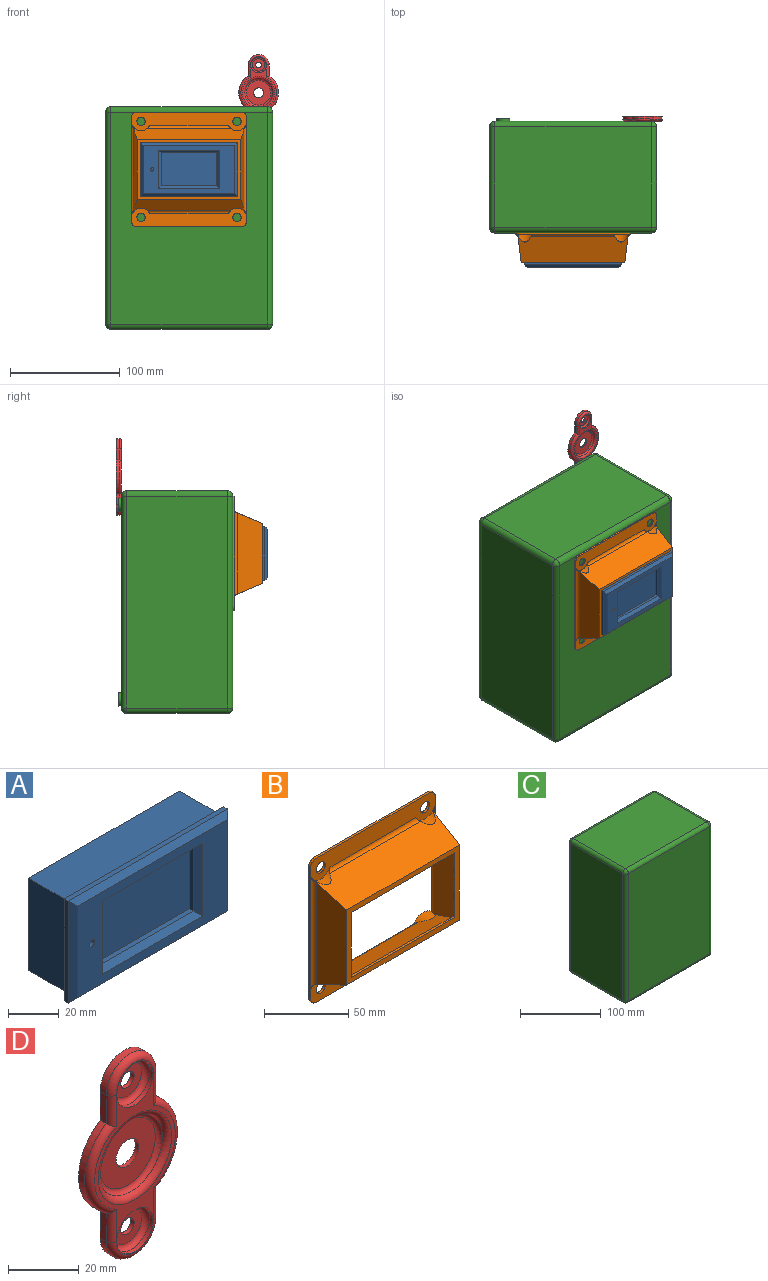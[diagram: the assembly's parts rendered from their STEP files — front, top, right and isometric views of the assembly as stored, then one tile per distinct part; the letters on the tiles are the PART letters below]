
ASSEMBLY  parts=4 mates=3
PART A: 26 faces, bbox 88.9x27x49.2 mm
  f0: plane 88.9x49.21mm, normal (0,1,0), area 635.1mm2, adj f2,f3,f4,f5,f12,f13,f14,f15
  f1: plane 83.82x44.13mm, normal (0,-1,0), area 1721.9mm2, adj f6,f18,f19,f20,f21,f22,f23,f24
  f2: plane 88.9x2.22mm, normal (0,0,1), area 197.6mm2, adj f0,f3,f5,f18
  f3: plane 49.21x2.22mm, normal (-1,0,0), area 109.4mm2, adj f0,f2,f4,f19
  f4: plane 88.9x2.22mm, normal (0,0,-1), area 197.6mm2, adj f0,f3,f5,f21
  f5: plane 49.21x2.22mm, normal (1,0,0), area 109.4mm2, adj f0,f2,f4,f20
  f6: cylinder r=1.59mm len=4.76mm, axis (0,-1,0), area 47.5mm2, adj f1,f17
  f7: plane 50.8x2.22mm, normal (0,0,-1), area 112.9mm2, adj f8,f10,f16,f22
  f8: plane 30.16x2.22mm, normal (1,0,0), area 67mm2, adj f7,f9,f16,f23
  f9: plane 50.8x2.22mm, normal (0,0,1), area 112.9mm2, adj f8,f10,f16,f25
  f10: plane 30.16x2.22mm, normal (-1,0,0), area 67mm2, adj f7,f9,f16,f24
  f11: plane 84.14x44.45mm, normal (0,1,0), area 3739.9mm2, adj f12,f13,f14,f15
  f12: plane 44.45x22.23mm, normal (-1,0,0), area 987.9mm2, adj f0,f11,f13,f15
  f13: plane 84.14x22.23mm, normal (0,0,-1), area 1870mm2, adj f0,f11,f12,f14
  f14: plane 44.45x22.23mm, normal (1,0,0), area 987.9mm2, adj f0,f11,f13,f15
  f15: plane 84.14x22.23mm, normal (0,0,1), area 1870mm2, adj f0,f11,f12,f14
  f16: plane 50.8x30.16mm, normal (0,-1,0), area 1532.3mm2, adj f7,f8,f9,f10
  f17: plane 3.18x3.18mm, normal (0,-1,0), area 7.9mm2, adj f6
  f18: plane 88.9x2.54mm, normal (0,-0.71,0.71), area 310.2mm2, adj f1,f2,f19,f20
  f19: plane 49.21x2.54mm, normal (-0.71,-0.71,0), area 167.7mm2, adj f1,f3,f18,f21
  f20: plane 49.21x2.54mm, normal (0.71,-0.71,0), area 167.7mm2, adj f1,f5,f18,f21
  f21: plane 88.9x2.54mm, normal (0,-0.71,-0.71), area 310.2mm2, adj f1,f4,f19,f20
  f22: plane 55.88x2.54mm, normal (0,-0.71,-0.71), area 191.6mm2, adj f1,f7,f23,f24
  f23: plane 35.24x2.54mm, normal (0.71,-0.71,0), area 117.5mm2, adj f1,f8,f22,f25
  f24: plane 35.24x2.54mm, normal (-0.71,-0.71,0), area 117.5mm2, adj f1,f10,f22,f25
  f25: plane 55.88x2.54mm, normal (0,-0.71,0.71), area 191.6mm2, adj f1,f9,f23,f24
PART B: 80 faces, bbox 104.8x27x104.8 mm
  f0: plane 87.76x19.75mm, normal (0,1,0), area 117.5mm2, adj f1,f62,f63,f64,f65,f67,f68,f73
  f1: plane 47.1x1.6mm, normal (1,0,0), area 70.4mm2, adj f0,f2,f3,f61,f63,f68,f69,f71
  f2: plane 94.6x54.6mm, normal (0,-1,0), area 1062.7mm2, adj f1,f9,f10,f21,f22,f61,f62,f63
  f3: plane 87.76x19.75mm, normal (0,1,0), area 117.5mm2, adj f1,f61,f62,f64,f66,f67,f69,f72
  f4: plane 8.2x8.2mm, normal (0,1,0), area 8.6mm2, adj f49,f77
  f5: plane 104.78x104.78mm, normal (0,1,0), area 648.7mm2, adj f13,f14,f15,f16,f17,f18,f19,f20
  f6: plane 8.2x8.2mm, normal (0,1,0), area 8.6mm2, adj f50,f79
  f7: plane 8.2x8.2mm, normal (0,1,0), area 8.6mm2, adj f51,f78
  f8: plane 104.78x17.23mm, normal (0,-1,0), area 1299.9mm2, adj f13,f14,f15,f17,f18,f25,f26,f29
  f9: plane 100.53x23.58mm, normal (0,-0.39,-0.92), area 2410.4mm2, adj f2,f21,f22,f25,f26,f28,f29,f30
  f10: plane 100.53x23.58mm, normal (0,-0.39,0.92), area 2410.4mm2, adj f2,f21,f22,f23,f24,f27,f28,f31
  f11: plane 104.78x17.23mm, normal (0,-1,0), area 1299.9mm2, adj f13,f15,f16,f19,f20,f23,f24,f27
  f12: plane 8.2x8.2mm, normal (0,1,0), area 8.6mm2, adj f48,f76
  f13: plane 94.78x1.6mm, normal (-1,0,0), area 151.6mm2, adj f5,f8,f11,f17,f20,f34
  f14: plane 94.78x1.6mm, normal (0,0,-1), area 151.6mm2, adj f5,f8,f17,f18
  f15: plane 94.78x1.6mm, normal (1,0,0), area 151.6mm2, adj f5,f8,f11,f18,f19,f28
  f16: plane 94.78x1.6mm, normal (0,0,1), area 151.6mm2, adj f5,f11,f19,f20
  f17: cylinder r=5mm len=5mm, axis (0,-1,0), area 12.6mm2, adj f5,f8,f13,f14
  f18: cylinder r=5mm len=5mm, axis (0,1,0), area 12.6mm2, adj f5,f8,f14,f15
  f19: cylinder r=5mm len=5mm, axis (0,-1,0), area 12.6mm2, adj f5,f11,f15,f16
  f20: cylinder r=5mm len=5mm, axis (0,1,0), area 12.6mm2, adj f5,f11,f13,f16
  f21: plane 74.02x22.84mm, normal (0.99,-0.12,0), area 1479.5mm2, adj f2,f9,f10,f28
  f22: plane 74.02x22.84mm, normal (-0.99,-0.12,0), area 1479.5mm2, adj f2,f9,f10,f34
  f23: cylinder r=8.61mm len=15.56mm, axis (0,1,0), area 68.5mm2, adj f10,f11,f27,f31
  f24: cylinder r=8.61mm len=15.56mm, axis (0,1,0), area 68.5mm2, adj f10,f11,f31,f32
  f25: cylinder r=8.61mm len=15.56mm, axis (0,1,0), area 68.5mm2, adj f8,f9,f30,f33
  f26: cylinder r=8.61mm len=15.56mm, axis (0,1,0), area 68.5mm2, adj f8,f9,f29,f30
  f27: cylinder r=3mm len=2.91mm, axis (-1,0,0), area 2.8mm2, adj f10,f11,f23,f28
  f28: cylinder r=3mm len=80.17mm, axis (0,0,-1), area 280.1mm2, adj f9,f10,f15,f21,f27,f29
  f29: cylinder r=3mm len=2.91mm, axis (1,0,0), area 2.8mm2, adj f8,f9,f26,f28
  f30: cylinder r=3mm len=76.14mm, axis (1,0,0), area 259.7mm2, adj f8,f9,f25,f26
  f31: cylinder r=3mm len=76.14mm, axis (-1,0,0), area 259.7mm2, adj f10,f11,f23,f24
  f32: cylinder r=3mm len=2.91mm, axis (-1,0,0), area 2.8mm2, adj f10,f11,f24,f34
  f33: cylinder r=3mm len=2.91mm, axis (1,0,0), area 2.8mm2, adj f8,f9,f25,f34
  f34: cylinder r=3mm len=80.17mm, axis (0,0,-1), area 280.1mm2, adj f9,f10,f13,f22,f32,f33
  f35: plane 101.58x17.23mm, normal (0,1,0), area 1146mm2, adj f36,f37,f43,f46,f47,f49,f51,f54
  f36: plane 94.78x0.52mm, normal (1,0,0), area 38mm2, adj f5,f35,f39,f44,f47,f55,f56,f60
  f37: plane 94.78x0.52mm, normal (-1,0,0), area 38mm2, adj f5,f35,f38,f39,f45,f46,f54,f57
  f38: cylinder r=4.6mm len=72.7mm, axis (0,0,-1), area 303.3mm2, adj f37,f52,f54,f57
  f39: plane 101.58x17.23mm, normal (0,1,0), area 1146mm2, adj f36,f37,f42,f44,f45,f48,f50,f56
  f40: plane 96.55x21.23mm, normal (0,0.39,0.92), area 2085.9mm2, adj f52,f53,f56,f57,f58,f64,f66,f67
  f41: plane 96.55x21.23mm, normal (0,0.39,-0.92), area 2085.9mm2, adj f52,f53,f54,f55,f59,f64,f65,f67
  f42: plane 94.78x0mm, normal (0,0,1), area 0mm2, adj f5,f39,f44,f45
  f43: plane 94.78x0mm, normal (0,0,-1), area 0mm2, adj f5,f35,f46,f47
  f44: cylinder r=3.4mm len=3.4mm, axis (0,-1,0), area 0mm2, adj f5,f36,f39,f42
  f45: cylinder r=3.4mm len=3.4mm, axis (0,1,0), area 0mm2, adj f5,f37,f39,f42
  f46: cylinder r=3.4mm len=3.4mm, axis (0,-1,0), area 0mm2, adj f5,f35,f37,f43
  f47: cylinder r=3.4mm len=3.4mm, axis (0,1,0), area 0mm2, adj f5,f35,f36,f43
  f48: cylinder r=4.1mm len=8.2mm, axis (0,-1,0), area 0mm2, adj f12,f39
  f49: cylinder r=4.1mm len=8.2mm, axis (0,-1,0), area 0mm2, adj f4,f35
  f50: cylinder r=4.1mm len=8.2mm, axis (0,-1,0), area 0mm2, adj f6,f39
  f51: cylinder r=4.1mm len=8.2mm, axis (0,-1,0), area 0mm2, adj f7,f35
  f52: plane 69.44x19.45mm, normal (-0.99,0.12,0), area 1221.9mm2, adj f38,f40,f41,f54,f57,f64
  f53: plane 69.44x19.45mm, normal (0.99,0.12,0), area 1221.9mm2, adj f40,f41,f55,f56,f60,f67
  f54: cylinder r=10.21mm len=16.53mm, axis (0,1,0), area 88.9mm2, adj f35,f37,f38,f41,f52,f59
  f55: cylinder r=10.21mm len=16.53mm, axis (0,1,0), area 88.9mm2, adj f35,f36,f41,f53,f59,f60
  f56: cylinder r=10.21mm len=16.53mm, axis (0,1,0), area 88.9mm2, adj f36,f39,f40,f53,f58,f60
  f57: cylinder r=10.21mm len=16.53mm, axis (0,1,0), area 88.9mm2, adj f37,f38,f39,f40,f52,f58
  f58: cylinder r=4.6mm len=74.67mm, axis (1,0,0), area 384.1mm2, adj f39,f40,f56,f57
  f59: cylinder r=4.6mm len=74.67mm, axis (-1,0,0), area 384.1mm2, adj f35,f41,f54,f55
  f60: cylinder r=4.6mm len=72.7mm, axis (0,0,-1), area 303.3mm2, adj f36,f53,f55,f56
  f61: plane 87.1x1.6mm, normal (0,0,1), area 139.4mm2, adj f1,f2,f3,f62
  f62: plane 47.1x1.6mm, normal (-1,0,0), area 70.4mm2, adj f0,f2,f3,f61,f63,f72,f73,f75
  f63: plane 87.1x1.6mm, normal (0,0,-1), area 139.4mm2, adj f0,f1,f2,f62
  f64: plane 54.17x2.24mm, normal (-0.66,0.75,0), area 134.3mm2, adj f0,f3,f40,f41,f52,f65,f66,f72
  f65: plane 90.87x2.08mm, normal (0,0.83,-0.55), area 222.5mm2, adj f0,f41,f64,f67
  f66: plane 90.87x2.08mm, normal (0,0.83,0.55), area 222.5mm2, adj f3,f40,f64,f67
  f67: plane 54.17x2.24mm, normal (0.66,0.75,0), area 134.3mm2, adj f0,f3,f40,f41,f53,f65,f66,f68
  f68: plane 2x1.98mm, normal (0,0,-1), area 2.2mm2, adj f0,f1,f67,f70,f71
  f69: plane 2x1.98mm, normal (0,0,1), area 2.2mm2, adj f1,f3,f67,f70,f71
  f70: plane 10x1.98mm, normal (1,0,0), area 19.8mm2, adj f67,f68,f69,f71
  f71: plane 10x2mm, normal (0,1,0), area 20mm2, adj f1,f68,f69,f70
  f72: plane 2x1.98mm, normal (0,0,1), area 2.2mm2, adj f3,f62,f64,f74,f75
  f73: plane 2x1.98mm, normal (0,0,-1), area 2.2mm2, adj f0,f62,f64,f74,f75
  f74: plane 10x1.98mm, normal (-1,0,0), area 19.8mm2, adj f64,f72,f73,f75
  f75: plane 10x2mm, normal (0,1,0), area 20mm2, adj f62,f72,f73,f74
  f76: cylinder r=3.75mm len=7.5mm, axis (0,-1,0), area 37.7mm2, adj f8,f12
  f77: cylinder r=3.75mm len=7.5mm, axis (0,-1,0), area 37.7mm2, adj f4,f11
  f78: cylinder r=3.75mm len=7.5mm, axis (0,-1,0), area 37.7mm2, adj f7,f11
  f79: cylinder r=3.75mm len=7.5mm, axis (0,-1,0), area 37.7mm2, adj f6,f8
PART C: 42 faces, bbox 152.4x104.6x203.2 mm
  f0: plane 193.2x91.6mm, normal (-1,0,0), area 17697.1mm2, adj f30,f35,f38,f41
  f1: plane 142.4x91.6mm, normal (0,0,-1), area 13043.8mm2, adj f27,f36,f37,f41
  f2: plane 193.2x91.6mm, normal (1,0,0), area 17697.1mm2, adj f22,f26,f27,f28
  f3: plane 142.4x91.6mm, normal (0,0,1), area 13043.8mm2, adj f22,f25,f29,f30
  f4: plane 193.2x142.4mm, normal (0,-1,0), area 27511.7mm2, adj f25,f26,f35,f36
  f5: plane 193.2x142.4mm, normal (0,1,0), area 27059.3mm2, adj f7,f10,f14,f19,f28,f29,f37,f38
  f6: cylinder r=1.59mm len=3.18mm, axis (0,-1,0), area 29.9mm2, adj f8,f9
  f7: cylinder r=6mm len=12mm, axis (0,-1,0), area 113.1mm2, adj f5,f8
  f8: plane 12x12mm, normal (0,1,0), area 105.2mm2, adj f6,f7
  f9: plane 3.18x3.18mm, normal (0,1,0), area 7.9mm2, adj f6
  f10: cylinder r=6mm len=12mm, axis (0,-1,0), area 113.1mm2, adj f5,f12
  f11: cylinder r=1.59mm len=3.18mm, axis (0,-1,0), area 29.9mm2, adj f12,f13
  f12: plane 12x12mm, normal (0,1,0), area 105.2mm2, adj f10,f11
  f13: plane 3.18x3.18mm, normal (0,1,0), area 7.9mm2, adj f11
  f14: cylinder r=6mm len=12mm, axis (0,-1,0), area 113.1mm2, adj f5,f16
  f15: cylinder r=1.59mm len=3.18mm, axis (0,-1,0), area 29.9mm2, adj f16,f17
  f16: plane 12x12mm, normal (0,1,0), area 105.2mm2, adj f14,f15
  f17: plane 3.18x3.18mm, normal (0,1,0), area 7.9mm2, adj f15
  f18: cylinder r=1.59mm len=3.18mm, axis (0,-1,0), area 29.9mm2, adj f20,f21
  f19: cylinder r=6mm len=12mm, axis (0,-1,0), area 113.1mm2, adj f5,f20
  f20: plane 12x12mm, normal (0,1,0), area 105.2mm2, adj f18,f19
  f21: plane 3.18x3.18mm, normal (0,1,0), area 7.9mm2, adj f18
  f22: cylinder r=5mm len=91.6mm, axis (0,-1,0), area 719.4mm2, adj f2,f3,f23,f24
  f23: sphere r=5mm, area 39.3mm2, adj f22,f25,f26
  f24: sphere r=5mm, area 39.3mm2, adj f22,f28,f29
  f25: cylinder r=5mm len=142.4mm, axis (1,0,0), area 1118.4mm2, adj f3,f4,f23,f31
  f26: cylinder r=5mm len=193.2mm, axis (0,0,-1), area 1517.4mm2, adj f2,f4,f23,f32
  f27: cylinder r=5mm len=91.6mm, axis (0,1,0), area 719.4mm2, adj f1,f2,f32,f33
  f28: cylinder r=5mm len=193.2mm, axis (0,0,1), area 1517.4mm2, adj f2,f5,f24,f33
  f29: cylinder r=5mm len=142.4mm, axis (-1,0,0), area 1118.4mm2, adj f3,f5,f24,f34
  f30: cylinder r=5mm len=91.6mm, axis (0,1,0), area 719.4mm2, adj f0,f3,f31,f34
  f31: sphere r=5mm, area 39.3mm2, adj f25,f30,f35
  f32: sphere r=5mm, area 39.3mm2, adj f26,f27,f36
  f33: sphere r=5mm, area 39.3mm2, adj f27,f28,f37
  f34: sphere r=5mm, area 39.3mm2, adj f29,f30,f38
  f35: cylinder r=5mm len=193.2mm, axis (0,0,1), area 1517.4mm2, adj f0,f4,f31,f39
  f36: cylinder r=5mm len=142.4mm, axis (-1,0,0), area 1118.4mm2, adj f1,f4,f32,f39
  f37: cylinder r=5mm len=142.4mm, axis (1,0,0), area 1118.4mm2, adj f1,f5,f33,f40
  f38: cylinder r=5mm len=193.2mm, axis (0,0,-1), area 1517.4mm2, adj f0,f5,f34,f40
  f39: sphere r=5mm, area 39.3mm2, adj f35,f36,f41
  f40: sphere r=5mm, area 39.3mm2, adj f37,f38,f41
  f41: cylinder r=5mm len=91.6mm, axis (0,-1,0), area 719.4mm2, adj f0,f1,f39,f40
PART D: 30 faces, bbox 39.3x4.4x71.4 mm
  f0: cylinder r=4.5mm len=9mm, axis (0,-1,0), area 39.6mm2, adj f6,f17
  f1: plane 9.95x2.4mm, normal (-1,0,0), area 23.9mm2, adj f6,f7,f16,f18
  f2: plane 9.95x2.4mm, normal (1,0,0), area 23.9mm2, adj f6,f7,f15,f21
  f3: plane 9.95x2.4mm, normal (-1,0,0), area 23.9mm2, adj f6,f8,f16,f22
  f4: plane 9.95x2.4mm, normal (1,0,0), area 23.9mm2, adj f6,f8,f15,f25
  f5: plane 65.85x32.3mm, normal (0,-1,0), area 284.8mm2, adj f9,f11,f18,f19,f20,f21,f22,f23
  f6: plane 69.85x36.3mm, normal (0,1,0), area 1521.1mm2, adj f0,f1,f2,f3,f4,f7,f8,f13
  f7: cylinder r=9.53mm len=19.05mm, axis (0,1,0), area 71.8mm2, adj f1,f2,f6,f19
  f8: cylinder r=9.53mm len=19.05mm, axis (0,1,0), area 71.8mm2, adj f3,f4,f6,f24
  f9: cylinder r=7.25mm len=14.5mm, axis (0,-1,0), area 63.8mm2, adj f5,f28
  f10: plane 11.3x11.3mm, normal (0,-1,0), area 77.9mm2, adj f14,f28
  f11: cylinder r=7.25mm len=14.5mm, axis (0,-1,0), area 63.8mm2, adj f5,f29
  f12: plane 11.3x11.3mm, normal (0,-1,0), area 77.9mm2, adj f13,f29
  f13: cylinder r=2.67mm len=5.33mm, axis (0,-1,0), area 23.5mm2, adj f6,f12
  f14: cylinder r=2.67mm len=5.33mm, axis (0,-1,0), area 23.5mm2, adj f6,f10
  f15: cylinder r=18.15mm len=30.9mm, axis (0,-1,0), area 88.7mm2, adj f2,f4,f6,f23
  f16: cylinder r=18.15mm len=30.9mm, axis (0,-1,0), area 88.7mm2, adj f1,f3,f6,f20
  f17: plane 22.3x22.3mm, normal (0,-1,0), area 327mm2, adj f0,f27
  f18: cylinder r=2mm len=11.11mm, axis (0,0,1), area 32.6mm2, adj f1,f5,f19,f20
  f19: torus R=7.52mm, axis (0,-1,0), area 86.8mm2, adj f5,f7,f18,f21
  f20: torus R=16.15mm, axis (0,-1,0), area 114mm2, adj f5,f16,f18,f22
  f21: cylinder r=2mm len=11.11mm, axis (0,0,-1), area 32.6mm2, adj f2,f5,f19,f23
  f22: cylinder r=2mm len=11.11mm, axis (0,0,1), area 32.6mm2, adj f3,f5,f20,f24
  f23: torus R=16.15mm, axis (0,-1,0), area 114mm2, adj f5,f15,f21,f25
  f24: torus R=7.52mm, axis (0,-1,0), area 86.8mm2, adj f5,f8,f22,f25
  f25: cylinder r=2mm len=11.11mm, axis (0,0,-1), area 32.6mm2, adj f4,f5,f23,f24
  f26: torus R=14.7mm, axis (0,-1,0), area 238.3mm2, adj f5,f27
  f27: torus R=11.15mm, axis (0,1,0), area 170.7mm2, adj f17,f26
  f28: torus R=5.65mm, axis (0,-1,0), area 105.3mm2, adj f9,f10
  f29: torus R=5.65mm, axis (0,-1,0), area 105.3mm2, adj f11,f12
PLACE A t=(-51.63,-3.21,64.82)mm
PLACE B t=(-59.57,23.79,-12.18)mm
PLACE C t=(-83.38,125.39,-105.75)mm
PLACE D t=(46.79,129.79,75.22)mm
MATE fastened D.f7 <-> C.f14  axis (0,-1,0) through (56.32,128.39,84.75)mm
MATE fastened C.f4 <-> B.f39  axis (0,-1,0) through (-7.18,23.79,-4.15)mm
MATE planar A.f16 <-> B.f2  axis (0,1,0) through (-7.18,-3.21,40.21)mm
